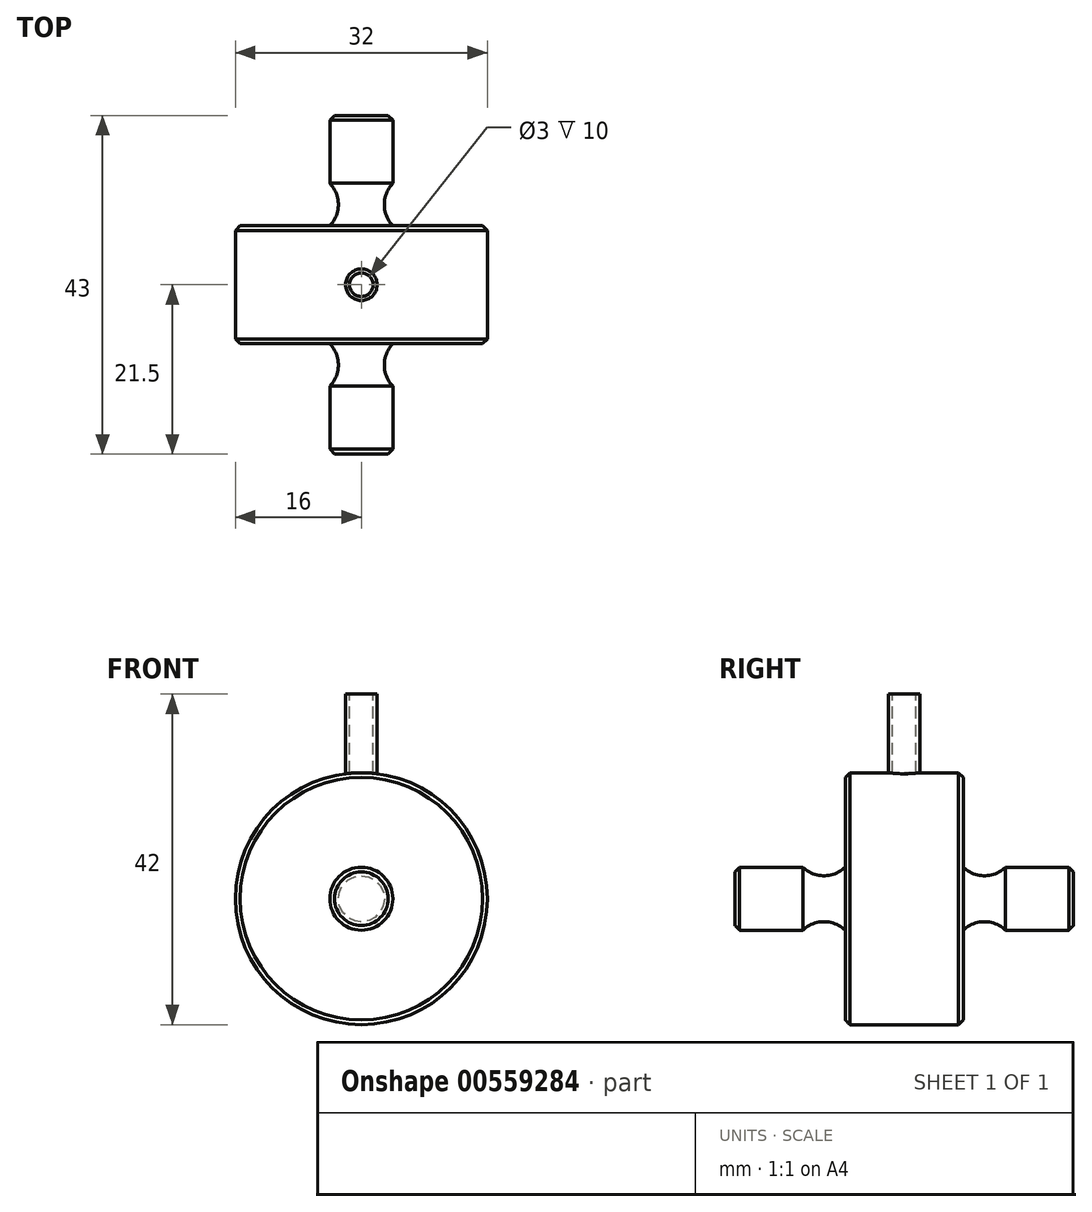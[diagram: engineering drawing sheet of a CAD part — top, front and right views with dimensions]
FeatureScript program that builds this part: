
annotation { "Feature Type Name" : "Feature", "Feature Type Description" : "" }
export const myFeature = defineFeature(function(context is Context, id is Id, definition is map)
    precondition{}
    {
        {
            var Q0;
            Q0=qCreatedBy(makeId("Top.planeOp"),FACE);
            var sketch = newSketch(context, id + "F0", { "sketchPlane" : qUnion([Q0])});
            skLineSegment(sketch, "E0", {"start": v(0, 0) * mm, "end": v(16, 0) * mm});
            skLineSegment(sketch, "E1", {"start": v(16, 0) * mm, "end": v(16, 7.5) * mm});
            skLineSegment(sketch, "E2", {"start": v(16, 7.5) * mm, "end": v(4, 7.5) * mm});
            skLineSegment(sketch, "E3", {"start": v(4, 12.88) * mm, "end": v(4, 21.5) * mm});
            skLineSegment(sketch, "E4", {"start": v(4, 21.5) * mm, "end": v(0, 21.5) * mm});
            skLineSegment(sketch, "E5", {"start": v(0, 21.5) * mm, "end": v(0, 0) * mm});
            skArc(sketch, "E6", {"start": v(4, 12.88) * mm, "mid": v(2.92, 10.19) * mm, "end": v(4, 7.5) * mm});
            skPoint(sketch, "E6.second.point", {"position": v(4, 12.88) * mm});
            skLineSegment(sketch, "E7.MirrorCS", {"start": v(4, -12.88) * mm, "end": v(4, -21.5) * mm});
            skLineSegment(sketch, "E8.MirrorCS", {"start": v(0, -21.5) * mm, "end": v(0, 0) * mm});
            skPoint(sketch, "E9.MirrorP", {"position": v(4, -12.88) * mm});
            skLineSegment(sketch, "E10.MirrorCS", {"start": v(16, 0) * mm, "end": v(16, -7.5) * mm});
            skLineSegment(sketch, "E11.MirrorCS", {"start": v(16, -7.5) * mm, "end": v(4, -7.5) * mm});
            skLineSegment(sketch, "E12.MirrorCS", {"start": v(4, -21.5) * mm, "end": v(0, -21.5) * mm});
            skArc(sketch, "E13.MirrorCS", {"start": v(4, -12.88) * mm, "mid": v(2.92, -10.19) * mm, "end": v(4, -7.5) * mm});
            skSolve(sketch);
        }
        {
            var Q0;
            Q0=makeQuery(id+"F0.imprint","IMPRINT",FACE,{"disambiguationData":[TD([[makeQuery(id+"F0.imprint","IMPRINT",EDGE,{"derivedFrom":sQuery(id+"F0.wireOp",EDGE,"E0")}),1.0]])]});
            var Q1;
            Q1=makeQuery(id+"F0.imprint","IMPRINT",FACE,{"disambiguationData":[TD([[makeQuery(id+"F0.imprint","IMPRINT",EDGE,{"derivedFrom":sQuery(id+"F0.wireOp",EDGE,"E0")}),-1.0]])]});
            var Q2;
            Q2=sQuery(id+"F0.wireOp",EDGE,"E5");
            revolve(context, id + "F1", {"entities" : qUnion([Q0, Q1]), "axis" : qUnion([Q2]), "revolveType" : RevolveType.FULL});
        }
        {
            var Q0;
            Q0=makeQuery(id+"F1.opRevolve","SWEPT_EDGE",EDGE,{"disambiguationData":[OSD([sQuery(id+"F0.wireOp",EDGE,"E3"),sQuery(id+"F0.wireOp",EDGE,"E4")])]});
            var Q1;
            Q1=makeQuery(id+"F1.opRevolve","SWEPT_EDGE",EDGE,{"disambiguationData":[OSD([sQuery(id+"F0.wireOp",EDGE,"E1"),sQuery(id+"F0.wireOp",EDGE,"E2")])]});
            var Q2;
            Q2=makeQuery(id+"F1.opRevolve","SWEPT_EDGE",EDGE,{"disambiguationData":[OSD([sQuery(id+"F0.wireOp",EDGE,"E10.MirrorCS"),sQuery(id+"F0.wireOp",EDGE,"E11.MirrorCS")])]});
            var Q3;
            Q3=makeQuery(id+"F1.opRevolve","SWEPT_EDGE",EDGE,{"disambiguationData":[OSD([sQuery(id+"F0.wireOp",EDGE,"E7.MirrorCS"),sQuery(id+"F0.wireOp",EDGE,"E12.MirrorCS")])]});
            chamfer(context, id + "F2", {"entities" : qUnion([Q0, Q1, Q2, Q3]), "width" : 0.6 * mm, "tangentPropagation" : true});
        }
        {
            var Q0;
            Q0=qCreatedBy(makeId("Top.planeOp"),FACE);
            var sketch = newSketch(context, id + "F3", { "sketchPlane" : qUnion([Q0])});
            skCircle(sketch, "E14", {"center": v(0, 0) * mm, "radius": 2 * mm});
            skSolve(sketch);
        }
        {
            var Q0;
            Q0 = qSketchRegion(id + "F3", true);
            extrude(context, id + "F4", {"entities" : qUnion([Q0]), "operationType" : NewBodyOperationType.ADD, "depth" : (42 - 16) * mm, "offsetDistance" : 25 * mm});
        }
        {
            var Q0;
            Q0=makeQuery(id+"F4.opExtrude","CAP_FACE",FACE,{"disambiguationData":[OSD([sQuery(id+"F3.wireOp",EDGE,"E14")])],"isStart":false});
            var sketch = newSketch(context, id + "F5", { "sketchPlane" : qUnion([Q0])});
            skCircle(sketch, "E15", {"center": v(0, 0) * mm, "radius": 1.5 * mm});
            skSolve(sketch);
        }
        {
            var Q0;
            Q0=makeQuery(id+"F5.imprint","IMPRINT",FACE,{"disambiguationData":[TD([[makeQuery(id+"F5.imprint","IMPRINT",EDGE,{"derivedFrom":sQuery(id+"F5.wireOp",EDGE,"E15")}),1.0]])]});
            extrude(context, id + "F6", {"entities" : qUnion([Q0]), "operationType" : NewBodyOperationType.REMOVE, "oppositeDirection" : true, "depth" : 10 * mm, "offsetDistance" : 25 * mm});
        }
    });
